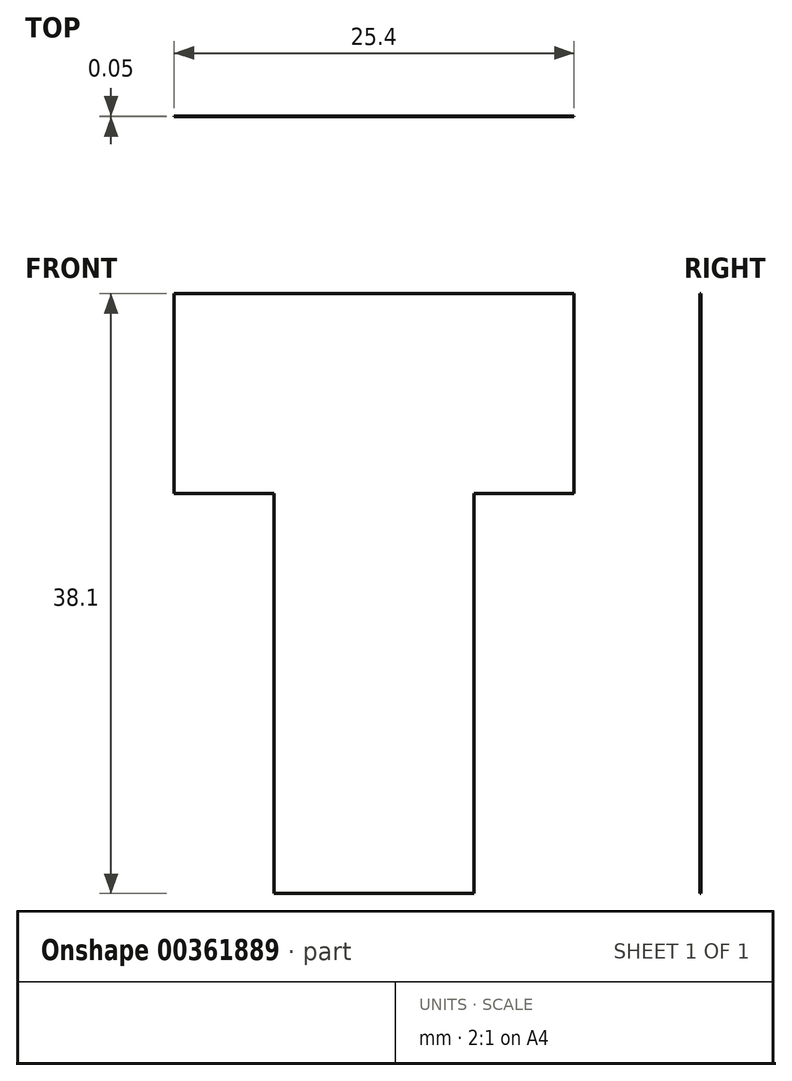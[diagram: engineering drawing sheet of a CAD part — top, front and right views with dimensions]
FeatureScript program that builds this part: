
annotation { "Feature Type Name" : "Feature", "Feature Type Description" : "" }
export const myFeature = defineFeature(function(context is Context, id is Id, definition is map)
    precondition{}
    {
        {
            var Q0;
            Q0=qCreatedBy(makeId("Front.planeOp"),FACE);
            var sketch = newSketch(context, id + "F0", { "sketchPlane" : qUnion([Q0])});
            skLineSegment(sketch, "E0", {"start": v(12.7, 0) * mm, "end": v(12.7, 25.4) * mm});
            skLineSegment(sketch, "E1", {"start": v(19.05, 25.4) * mm, "end": v(19.05, 38.1) * mm});
            skLineSegment(sketch, "E2", {"start": v(19.05, 38.1) * mm, "end": v(-6.35, 38.1) * mm});
            skLineSegment(sketch, "E3", {"start": v(-6.35, 38.1) * mm, "end": v(-6.35, 25.4) * mm});
            skLineSegment(sketch, "E4", {"start": v(0, 0) * mm, "end": v(0, 25.4) * mm});
            skLineSegment(sketch, "E5", {"start": v(-6.35, 25.4) * mm, "end": v(0, 25.4) * mm});
            skLineSegment(sketch, "E6", {"start": v(19.05, 25.4) * mm, "end": v(12.7, 25.4) * mm});
            skLineSegment(sketch, "E7", {"start": v(0, 0) * mm, "end": v(12.7, 0) * mm});
            skSolve(sketch);
        }
        {
            var Q0;
            Q0=makeQuery(id+"F0.imprint","IMPRINT",FACE,{"disambiguationData":[TD([[makeQuery(id+"F0.imprint","IMPRINT",EDGE,{"derivedFrom":sQuery(id+"F0.wireOp",EDGE,"E0")}),1.0]])]});
            extrude(context, id + "F1", {"entities" : qUnion([Q0]), "depth" : 5 / 101.6 * mm});
        }
    });
